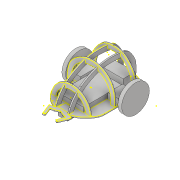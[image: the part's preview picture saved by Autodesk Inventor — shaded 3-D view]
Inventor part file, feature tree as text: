
AUTODESK INVENTOR PART (.ipt)
format: ipt  version: 2019 (Build 230136000, 136)  size: 612,352 bytes
history: native  units: mm
features: sketch x18, extrude x12, plane x8, projected_geometry x7, revolve x2, mirror x1
ambient origin geometry x8: Origin, YZ Plane, XZ Plane, XY Plane, X Axis, Y Axis, Z Axis, Center Point
bodies: Solid1 (feature_tree)
feature tree (48):
  sketch  "Sketch1"  dims[d0=83.15mm d1=55.3mm]
  extrude  "Extrusion1"  Depth=55.3mm
  extrude  "Extrusion2"  Depth=48.8mm
  extrude  "Extrusion3"  Depth=6.0mm
  extrude  "Extrusion4"  Depth=30.0mm
  extrude  "Extrusion5"  Depth=20.32mm
  extrude  "Extrusion6"  Depth=2.0mm
  extrude  "Extrusion7"  Depth=2.0mm
  plane  "Work Plane1"
  sketch  "Sketch3"  dims[d9=10.0mm d12=6.0mm]
  revolve  "Revolution1"  [1 undecoded]
  revolve  "Revolution2"  [1 undecoded]
  sketch  "Sketch5"  dims[d14=30.0mm d15=30.0mm]
  plane  "Work Plane3"
  sketch  "Sketch6"  dims[d16=8.15mm d17=20.32mm]
  plane  "Work Plane4"
  extrude  "Extrusion8"  Depth=25.0mm
  mirror  "Mirror1"
  sketch  "Sketch8"  dims[d21=2.0mm d22=2.0mm]
  plane  "Work Plane5"
  plane  "Work Plane6"
  plane  "Work Plane7"
  sketch  "Sketch10"  dims[d24=5.0mm d25=15.24mm]
  sketch  "Sketch11"  dims[d26=28.5mm d27=2.0mm]
  plane  "Work Plane8"
  extrude  "Extrusion10"  Depth=16.9mm TaperAngle=0.0deg
  plane  "Work Plane9"
  extrude  "Extrusion14"  Depth=16.637mm TaperAngle=0.0deg
  extrude  "Extrusion15"  Depth=12.8mm TaperAngle=0.0deg
  extrude  "Extrusion16"  Depth=12.8mm
  sketch  "Sketch20"  dims[d49=12.8mm d50=0.0mm d51=6.4mm]
  sketch  "Sketch21"  dims[d52=90.0deg]
  sketch  "Sketch22"  dims[d53=90.0deg]
  sketch  "Sketch23"  dims[d54=68.703586mm]
  sketch  "Sketch24"  dims[d55=5.0mm d56=68.703586mm d57=25.0mm d58=2.0mm d64=9.0mm d65=3.175mm d66=2.0mm d67=9.525mm d68=10.0mm d69=5.0mm d70=9.525mm d71=13.7475mm d72=13.748mm d73=3.048mm d74=0.0mm d75=3.175mm d76=9.0mm d77=9.525mm d78=15.0mm d79=9.525mm d80=3.175mm d81=4.0mm d82=9.525mm d83=3.175mm d84=5.0mm d85=9.0mm d86=13.75mm d87=1.848179mm d88=-1.848mm d89=4.376821mm d90=4.377mm d91=10.5875mm d100=32.315mm d103=3.048mm d104=0.0mm d116=9.525mm d119=42.0mm d121=3.048mm d122=0.0mm d124=42.0mm d125=7.0mm d126=9.525mm d127=7.0mm d128=3.048mm d129=0.0mm d130=10.0mm d131=5.0mm d132=20.0mm d133=25.0mm d134=5.0mm d135=1.0mm d136=3.175mm d137=0.0mm]
  sketch  "Sketch2"  dims[d7=26.0mm d8=48.8mm]
  sketch  "Sketch7"  dims[d18=14.732mm d19=2.0mm]
  sketch  "Sketch13"  dims[d28=5.0mm d34=25.0mm]
  sketch  "Sketch16"  dims[d37=3.175mm d38=0.0mm d39=16.9mm d40=0.0mm]
  sketch  "Sketch17"  dims[d41=10.0mm d42=0.0mm d43=16.637mm d44=0.0mm]
  sketch  "Sketch18"  dims[d45=1.75mm d46=0.0mm d47=12.8mm d48=0.0mm]
  projected_geometry  "Projected Loop1"
  projected_geometry  "Projected Loop2"
  projected_geometry  "Projected Loop3"
  projected_geometry  "Projected Loop4"
  projected_geometry  "Projected Loop5"
  projected_geometry  "Projected Loop6"
  projected_geometry  "Projected Loop7"
note: 2 required parameter values undecoded (feature->parameter linkage not recoverable at this tier; creation-order binding heuristic only, values carry confidence <= 0.55)
